# Revit family: NLRS_57_AIR_UN_Swirl-diffuser-rrfoo-return_LT_sacs
name_source: partatom
category: Air Terminals
units: mm (PartAtom-declared; Revit-internal decimal feet)

## family parameters
Always vertical = Yes
Cut with Voids When Loaded = No
Part Type = Normal
Room Calculation Point = No
Round Connector Dimension = Use Diameter
Shared = No
Work Plane-Based = No

## types (5) — shared parameters
Assembly Code = 57.00
Description = Round flanged Swirl return grill, Type RRFO
Flip_Connector_to_left = No
IfcDescription = Round flanged Swirl return grill, Type RRFO
IfcExportAs = IfcAirterminal
IfcExportType = Diffuser
Manufacturer = Solid Air Climate Solutions
NLRS_C_content_datum_uitgifte = 13-08-2025
NLRS_C_content_provider = Solid Air Climate Solutions
NLRS_C_content_versie = 4.22.00
NLRS_C_description = Round flanged Swirl return grill, Type RRFO
SACS_Custom_Color_1 = NLRS_57_ral 9010-55_gen_sacs
SACS_Data_Hidden = RRFO_Data
SACS_Data_Hidden2 = RRFO_factors
URL = https://solid-air.nl
zero-valued in all types: Default Elevation

## per-type parameters (varying)
| type | Max Flow | Min Flow | SACS_Base_Index | SACS_Diameter2 | SACS_Factor_LpF1 | SACS_Factor_LpF2 | SACS_Factor_PsF1 | SACS_Factor_PsF2 | SACS_Offset1 | SACS_Radius_1 | SACS_Radius_2 | SACS_Radius_3 |
| 125 | 144.0 m³/h | 54.0 m³/h | 1 | 124 mm  [stored 0.406824 ft] | -108.200146 | 29.575267 | 958.509852 | 1.828498 | 22 mm  [stored 0.0721785 ft] | 16.05 mm  [stored 0.0526575 ft] | 60.5 mm  [stored 0.198491 ft] | 102.5 mm  [stored 0.336286 ft] |
| 160 | 288.0 m³/h | 108.0 m³/h | 2 | 158 mm | -128.442504 | 30.452739 | 128.966251 | 1.988041 | 27 mm  [stored 0.0885827 ft] | 20.3 mm  [stored 0.066601 ft] | 77.5 mm  [stored 0.254265 ft] | 125 mm  [stored 0.410105 ft] |
| 200 | 450.0 m³/h | 144.0 m³/h | 3 | 198 mm  [stored 0.649606 ft] | -136.871155 | 30.040249 | 28.108028 | 2.035456 | 32 mm  [stored 0.104987 ft] | 25.15 mm  [stored 0.0825131 ft] | 97.9 mm  [stored 0.321194 ft] | 155 mm  [stored 0.50853 ft] |
| 250 | 720.0 m³/h | 216.0 m³/h | 4 | 249 mm  [stored 0.816929 ft] | -161.20111 | 31.92384 | 16.412962 | 1.974918 | 42 mm  [stored 0.137795 ft] | 32.05 mm  [stored 0.105151 ft] | 122.15 mm  [stored 0.400755 ft] | 190 mm |
| 315 | 1080.0 m³/h | 360.0 m³/h | 5 | 313.5 mm  [stored 1.02854 ft] | -163.716478 | 30.147475 | 4.835403 | 2.01778 | 42 mm  [stored 0.137795 ft] | 35.15 mm  [stored 0.115322 ft] | 156 mm  [stored 0.511811 ft] | 217.5 mm  [stored 0.713583 ft] |

note: [stored X ft] marks values corroborated as IEEE doubles in the binary element streams (Revit-internal decimal feet)

## geometry (parser evidence)
native form markers: Sweep x11
no freeform markers — native parametric forms only
